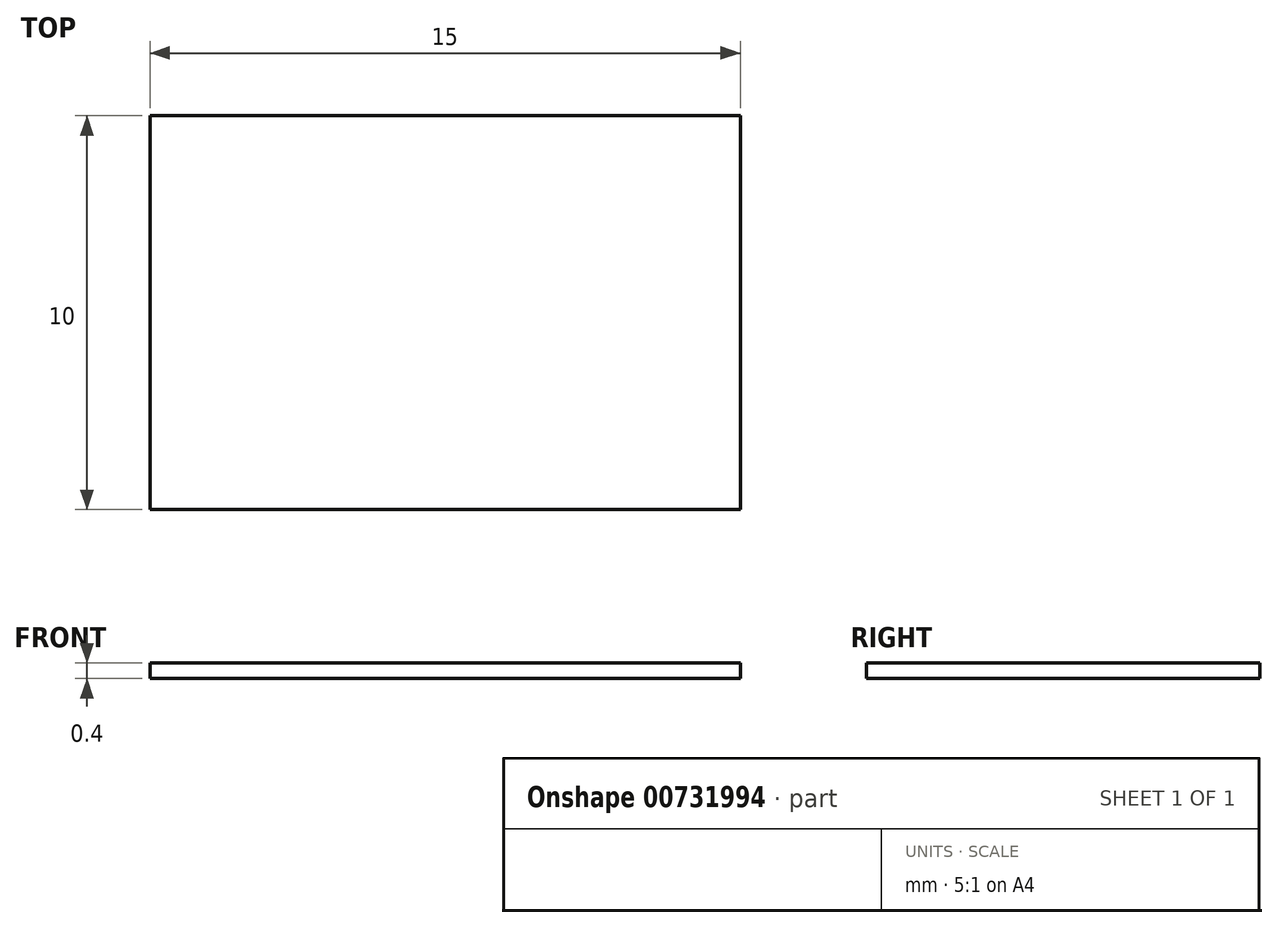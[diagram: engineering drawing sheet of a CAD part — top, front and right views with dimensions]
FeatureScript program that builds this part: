
annotation { "Feature Type Name" : "Feature", "Feature Type Description" : "" }
export const myFeature = defineFeature(function(context is Context, id is Id, definition is map)
    precondition{}
    {
        {
            var Q0;
            Q0=qCreatedBy(makeId("Top.planeOp"),FACE);
            var sketch = newSketch(context, id + "F0", { "sketchPlane" : qUnion([Q0])});
            skLineSegment(sketch, "E0.bottom", {"start": v(0, 0) * mm, "end": v(15, 0) * mm});
            skLineSegment(sketch, "E0.top", {"start": v(0, 10) * mm, "end": v(15, 10) * mm});
            skLineSegment(sketch, "E0.left", {"start": v(0, 0) * mm, "end": v(0, 10) * mm});
            skLineSegment(sketch, "E0.right", {"start": v(15, 0) * mm, "end": v(15, 10) * mm});
            skSolve(sketch);
        }
        {
            var Q0;
            Q0 = qSketchRegion(id + "F0", true);
            extrude(context, id + "F1", {"entities" : qUnion([Q0]), "depth" : .4 * mm, "offsetDistance" : 25 * mm});
        }
    });
